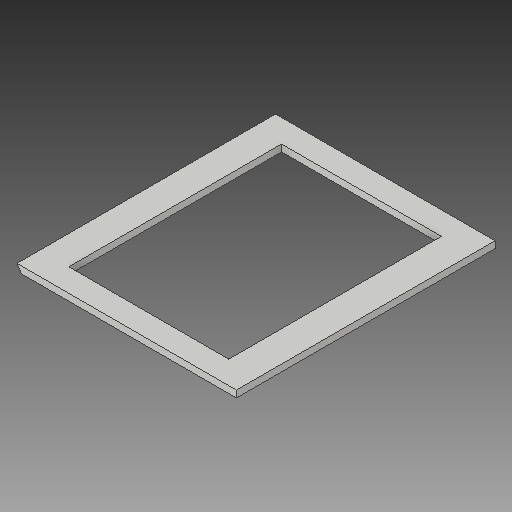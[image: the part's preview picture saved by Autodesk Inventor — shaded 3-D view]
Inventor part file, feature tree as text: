
AUTODESK INVENTOR PART (.ipt)
format: ipt  version: 2017 (Build 210142000, 142)  size: 112,128 bytes
history: native  units: in
note: dims shown in document units (in); Inventor stores cm internally (conversion verified against a paired STEP export)
features: extrude x3, sketch x3, other x3, reference x1
ambient origin geometry x8: Origin, YZ Plane, XZ Plane, XY Plane, X Axis, Y Axis, Z Axis, Center Point
bodies: Solid1 (feature_tree)
feature tree (10):
  extrude  "Extrusion1"  Depth=9.5in
  extrude  "Extrusion2"  Depth=5.875in
  extrude  "Extrusion4"  Depth=0.8438in
  sketch  "Sketch1"  dims[d0=8.0625in d1=9.5in]
  sketch  "Sketch2"  dims[d2=0.25in d3=0.0in d4=5.875in]
  sketch  "Sketch4"  dims[d5=7.8125in d6=0.8438in d7=1.0625in d8=1.0in d9=0.0in d12=9.5in d13=0.0in]
  reference  "Reference2"
  parser-record x1  (decoder bookkeeping rows leaked as tree rows — omitted from the tree; the rows remain in map.json)
  other  "Arcade.iam"
  other  "front_screen_footer:1"
note: 1 file-system path scrubbed to <path> (originals preserved in map.json)
